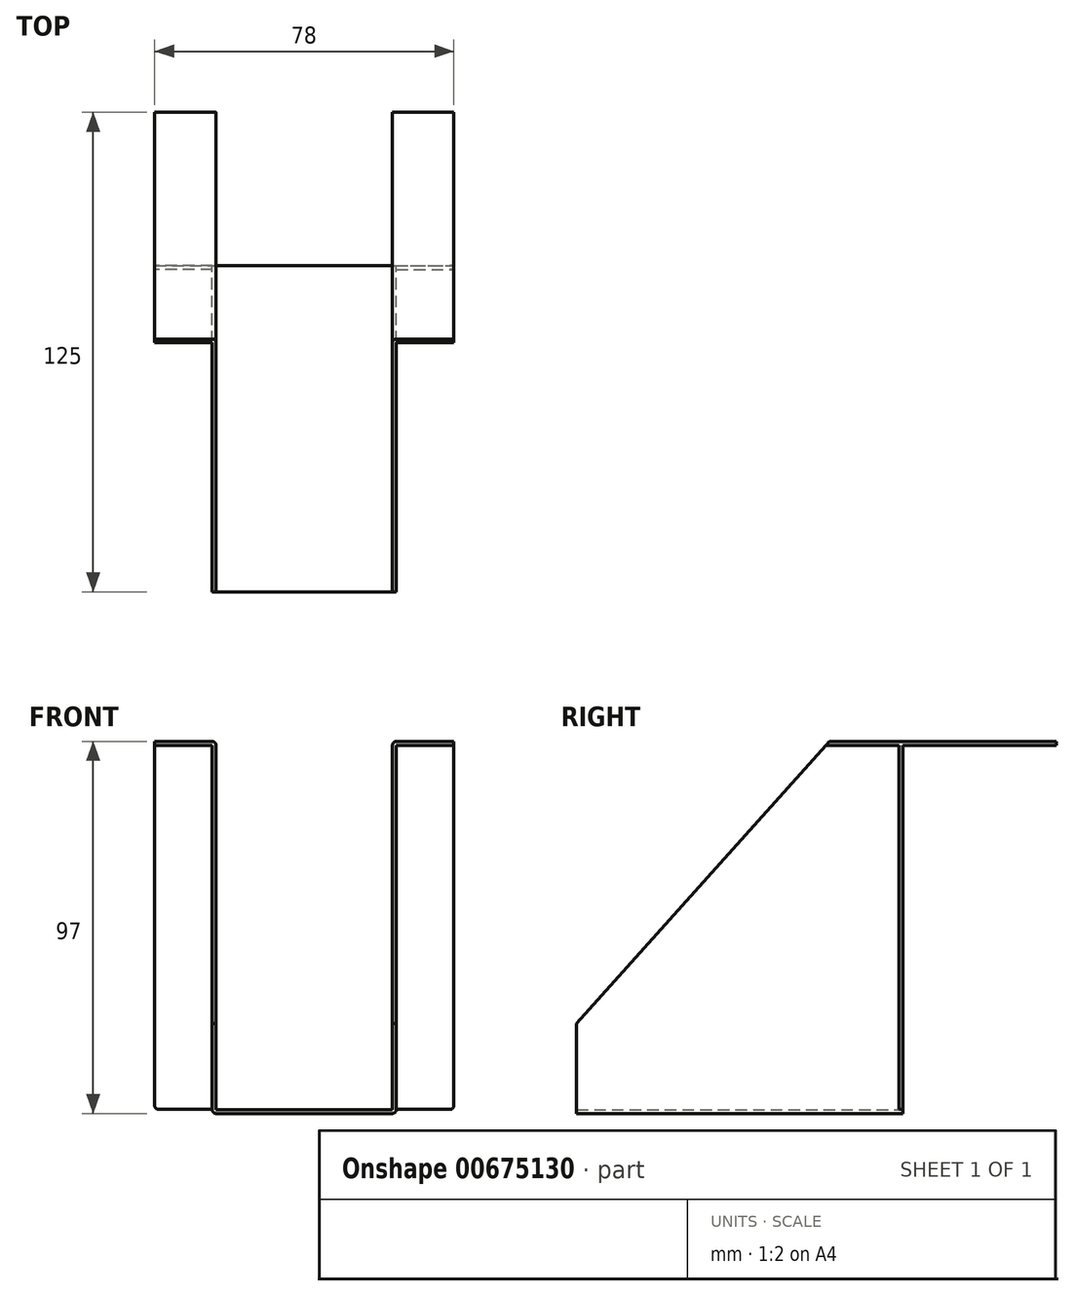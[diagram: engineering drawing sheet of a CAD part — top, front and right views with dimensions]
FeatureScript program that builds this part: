
annotation { "Feature Type Name" : "Feature", "Feature Type Description" : "" }
export const myFeature = defineFeature(function(context is Context, id is Id, definition is map)
    precondition{}
    {
        {
            var Q0;
            Q0=qCreatedBy(makeId("Front.planeOp"),FACE);
            var sketch = newSketch(context, id + "F0", { "sketchPlane" : qUnion([Q0])});
            skLineSegment(sketch, "E0", {"start": v(1, 0) * mm, "end": v(47, 0) * mm});
            skLineSegment(sketch, "E1", {"start": v(48, 1) * mm, "end": v(48, 96) * mm});
            skLineSegment(sketch, "E2", {"start": v(48, 96) * mm, "end": v(63, 96) * mm});
            skLineSegment(sketch, "E3", {"start": v(24, 0) * mm, "end": v(24, 88.93) * mm, "construction": true});
            skLineSegment(sketch, "E4.MirrorCS", {"start": v(0, 1) * mm, "end": v(0, 96) * mm});
            skLineSegment(sketch, "E5.MirrorCS", {"start": v(0, 96) * mm, "end": v(-15, 96) * mm});
            skLineSegment(sketch, "E6.0", {"start": v(0, 97) * mm, "end": v(-15, 97) * mm});
            skLineSegment(sketch, "E6.1", {"start": v(48, 97) * mm, "end": v(63, 97) * mm});
            skLineSegment(sketch, "E6.2", {"start": v(47, 1) * mm, "end": v(47, 96) * mm});
            skLineSegment(sketch, "E6.3", {"start": v(1, 1) * mm, "end": v(47, 1) * mm});
            skLineSegment(sketch, "E6.4", {"start": v(1, 1) * mm, "end": v(1, 96) * mm});
            skLineSegment(sketch, "E7", {"start": v(-15, 97) * mm, "end": v(-15, 96) * mm});
            skPoint(sketch, "E8.visualSharp", {"position": v(1, 97) * mm});
            skArc(sketch, "E8.filletArc", {"start": v(1, 96) * mm, "mid": v(0.7, 96.7) * mm, "end": v(0, 97) * mm});
            skPoint(sketch, "E9.visualSharp", {"position": v(47, 97) * mm});
            skArc(sketch, "E9.filletArc", {"start": v(48, 97) * mm, "mid": v(47.3, 96.7) * mm, "end": v(47, 96) * mm});
            skPoint(sketch, "E10.visualSharp", {"position": v(48, 0) * mm});
            skArc(sketch, "E10.filletArc", {"start": v(47, 0) * mm, "mid": v(47.7, 0.3) * mm, "end": v(48, 1) * mm});
            skPoint(sketch, "E11.visualSharp", {"position": v(0, 0) * mm});
            skArc(sketch, "E11.filletArc", {"start": v(0, 1) * mm, "mid": v(0.3, 0.3) * mm, "end": v(1, 0) * mm});
            skLineSegment(sketch, "E12", {"start": v(63, 96) * mm, "end": v(63, 97) * mm});
            skSolve(sketch);
        }
        {
            var Q0;
            Q0 = qSketchRegion(id + "F0", true);
            extrude(context, id + "F1", {"entities" : qUnion([Q0]), "depth" : 125 * mm, "offsetDistance" : 25 * mm});
        }
        {
            var Q0;
            Q0=makeQuery(id+"F1.opExtrude","SWEPT_FACE",FACE,{"disambiguationData":[OSD([sQuery(id+"F0.wireOp",EDGE,"E12")])]});
            var sketch = newSketch(context, id + "F2", { "sketchPlane" : qUnion([Q0])});
            skCircle(sketch, "E13", {"center": v(0, 97) * mm, "radius": 40 * mm, "construction": true});
            skCircle(sketch, "E14", {"center": v(-40, 97) * mm, "radius": 20 * mm, "construction": true});
            skCircle(sketch, "E15", {"center": v(-125, 0.98) * mm, "radius": 10 * mm, "construction": true});
            skLineSegment(sketch, "E16", {"start": v(0, 96) * mm, "end": v(-59.97, 96) * mm, "construction": true});
            skLineSegment(sketch, "E17.bottom", {"start": v(-39.99, 96) * mm, "end": v(5.35, 96) * mm});
            skLineSegment(sketch, "E17.top", {"start": v(-39.99, -3.64) * mm, "end": v(5.35, -3.64) * mm});
            skLineSegment(sketch, "E17.left", {"start": v(-39.99, 96) * mm, "end": v(-39.99, -3.64) * mm});
            skLineSegment(sketch, "E17.right", {"start": v(5.35, 96) * mm, "end": v(5.35, -3.64) * mm});
            skLineSegment(sketch, "E18", {"start": v(-139.87, 6.79) * mm, "end": v(-55.96, 100.48) * mm});
            skLineSegment(sketch, "E19", {"start": v(-139.87, 6.79) * mm, "end": v(-139.87, 100.48) * mm});
            skLineSegment(sketch, "E20", {"start": v(-55.96, 100.48) * mm, "end": v(-139.87, 100.48) * mm});
            skPoint(sketch, "E21.orphan", {"position": v(-139.87, 96) * mm});
            skSolve(sketch);
        }
        {
            var Q0;
            Q0 = qSketchRegion(id + "F2", true);
            extrude(context, id + "F3", {"entities" : qUnion([Q0]), "operationType" : NewBodyOperationType.REMOVE, "oppositeDirection" : true, "depth" : 100 * mm, "offsetDistance" : 25 * mm, "hasSecondDirection" : true, "secondDirectionOppositeDirection" : false, "secondDirectionDepth" : 50 * mm});
        }
        {
            var Q0;
            Q0=makeQuery(id+"F3.boolean.opBoolean","COPY",FACE,{"derivedFrom":makeQuery(id+"F3.opExtrude","SWEPT_FACE",FACE,{"disambiguationData":[OSD([sQuery(id+"F2.wireOp",EDGE,"E17.left")])]})});
            var sketch = newSketch(context, id + "F4", { "sketchPlane" : qUnion([Q0])});
            skLineSegment(sketch, "E22.bottom", {"start": v(-47, 96) * mm, "end": v(-63, 96) * mm});
            skLineSegment(sketch, "E22.left", {"start": v(-47, 96) * mm, "end": v(-47, 1.06) * mm});
            skLineSegment(sketch, "E22.right", {"start": v(-63, 96) * mm, "end": v(-63, 2.06) * mm});
            skLineSegment(sketch, "E23", {"start": v(-47, 1.06) * mm, "end": v(-62, 1.06) * mm});
            skPoint(sketch, "E24.orphan", {"position": v(-63, 0) * mm});
            skPoint(sketch, "E25.visualSharp", {"position": v(-63, 1.06) * mm});
            skArc(sketch, "E25.filletArc", {"start": v(-63, 2.06) * mm, "mid": v(-62.7, 1.36) * mm, "end": v(-62, 1.06) * mm});
            skLineSegment(sketch, "E26", {"start": v(-24, 1) * mm, "end": v(-24, 15.87) * mm, "construction": true});
            skLineSegment(sketch, "E27.MirrorCS", {"start": v(15, 96) * mm, "end": v(15, 2.06) * mm});
            skArc(sketch, "E28.MirrorCS", {"start": v(15, 2.06) * mm, "mid": v(14.7, 1.36) * mm, "end": v(14, 1.06) * mm});
            skLineSegment(sketch, "E29.MirrorCS", {"start": v(-1, 1.06) * mm, "end": v(14, 1.06) * mm});
            skLineSegment(sketch, "E30.MirrorCS", {"start": v(-1, 96) * mm, "end": v(-1, 1.06) * mm});
            skLineSegment(sketch, "E31.MirrorCS", {"start": v(-1, 96) * mm, "end": v(15, 96) * mm});
            skSolve(sketch);
        }
        {
            var Q0;
            {var subQ1=sQuery(id+"F4.wireOp",EDGE,"E22.right");Q0=makeQuery(id+"F4.imprint","IMPRINT",FACE,{"disambiguationData":[TD([[makeQuery(id+"F4.imprint","IMPRINT",EDGE,{"derivedFrom":subQ1}),1.0]])]});}
            var Q1;
            {var subQ6=sQuery(id+"F4.wireOp",EDGE,"E27.MirrorCS");Q1=makeQuery(id+"F4.imprint","IMPRINT",FACE,{"disambiguationData":[TD([[makeQuery(id+"F4.imprint","IMPRINT",EDGE,{"derivedFrom":subQ6}),-1.0]])]});}
            extrude(context, id + "F5", {"entities" : qUnion([Q0, Q1]), "operationType" : NewBodyOperationType.ADD, "oppositeDirection" : true, "depth" : 1 * mm, "offsetDistance" : 25 * mm});
        }
    });
